SOLIDWORKS PART (.sldprt)
format: sldprt  version: not decoded by parser v0  size: 144,896 bytes
history: native  units: mm
features: plane x3, sketch x2, material x1, extrude x1, chamfer x1, cut_extrude x1 (+11 scaffold rows collapsed)
feature tree (20):
  scaffold x11  (default folders/planes/origin — collapsed)
  material  "Matériau <non spécifié>"
  plane  "Face"
  plane  "Dessus"
  plane  "Droite"
  sketch  "Esquisse1"  dims[D1=6.0mm D2=4.0mm]
  extrude  "Extrusion1"  Depth=14mm
  chamfer  "Chanfrein1"  Distance=0.25mm Angle=45deg
  sketch  "Esquisse4"  dims[D1=0.25mm D2=0.25mm D3=0.25mm]
  cut_extrude  "Enlèv. mat.-Extru.1"  Depth=10mm
decode coverage: 5 of 5 modeling features carry decoded parameters
note: suppression state not decoded; provenance and decode notes live in map.json
